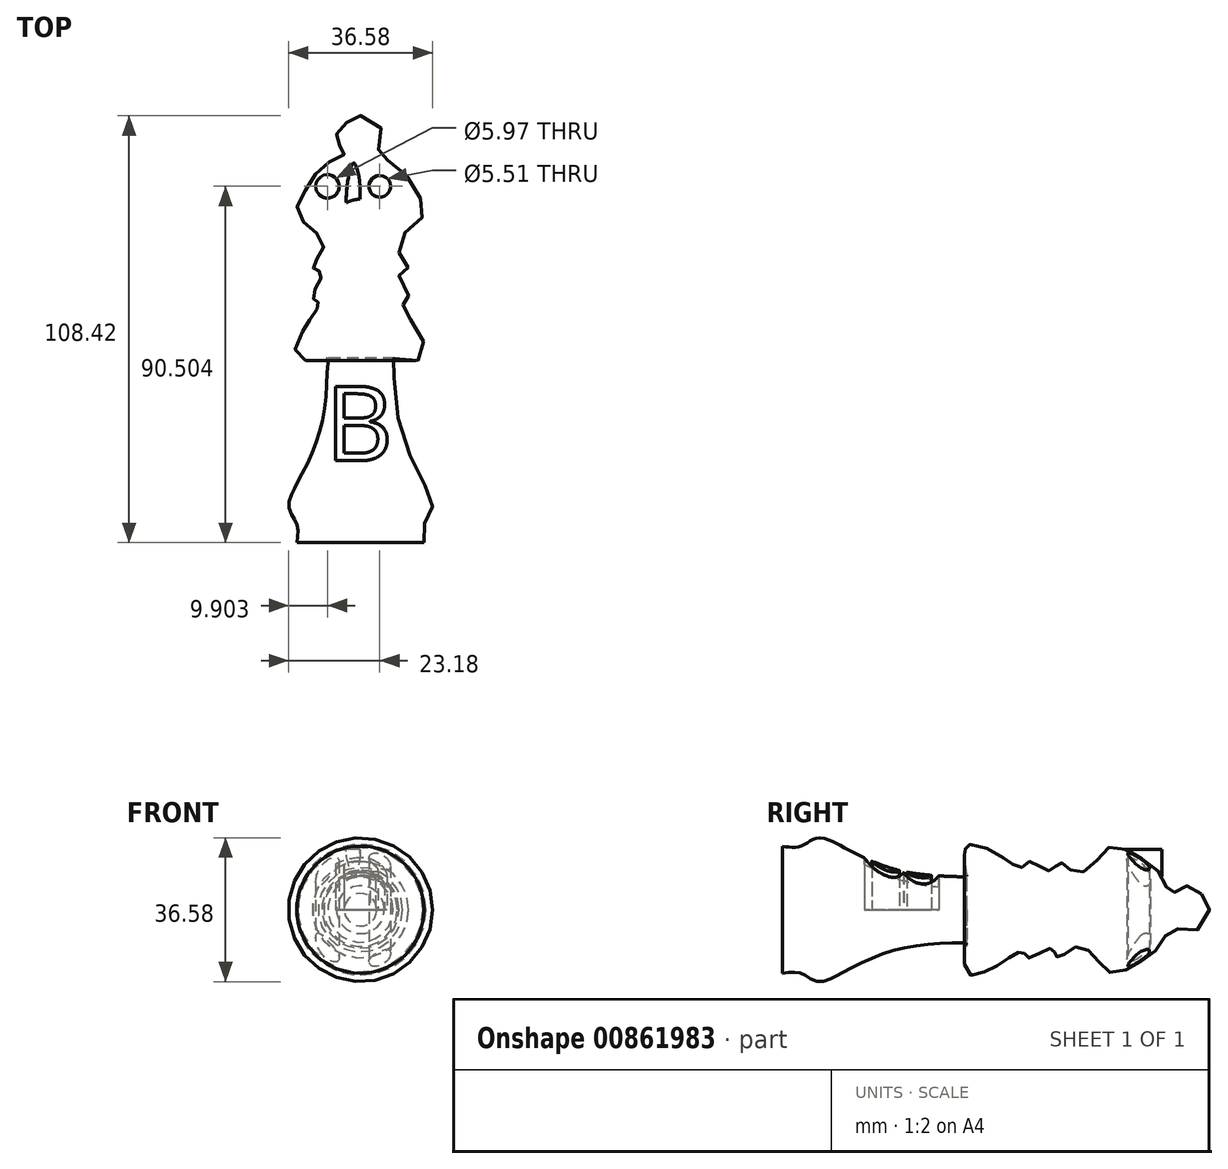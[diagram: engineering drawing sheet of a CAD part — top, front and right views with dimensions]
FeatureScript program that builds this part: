
annotation { "Feature Type Name" : "Feature", "Feature Type Description" : "" }
export const myFeature = defineFeature(function(context is Context, id is Id, definition is map)
    precondition{}
    {
        {
            var Q0;
            Q0=qCreatedBy(makeId("Top.planeOp"),FACE);
            var sketch = newSketch(context, id + "F0", { "sketchPlane" : qUnion([Q0])});
            skLineSegment(sketch, "E0", {"start": v(-40.03, 64.77) * mm, "end": v(-40.03, -59.56) * mm});
            skLineSegment(sketch, "E1", {"start": v(-40.03, -49.87) * mm, "end": v(-23.88, -49.87) * mm});
            skFitSpline(sketch, "E2", {"points": [v(-23.88, -49.87) * mm, v(-23.88, -45.26) * mm, v(-21.8, -41.1) * mm, v(-23.88, -34.88) * mm, v(-30.34, -18.96) * mm, v(-31.72, -3.74) * mm, v(-31.5, -3.05) * mm, v(-23.88, -3.05) * mm, v(-26.19, 5.26) * mm, v(-28.26, 8.26) * mm, v(-29.19, 11.26) * mm, v(-27.8, 12.4) * mm, v(-30.1, 17.71) * mm, v(-29.65, 19.1) * mm, v(-27.8, 20.25) * mm, v(-30.57, 24.63) * mm, v(-27.57, 29.94) * mm, v(-23.88, 33.86) * mm, v(-26.42, 40.32) * mm, v(-31.96, 46.78) * mm, v(-35.88, 48.85) * mm, v(-34.03, 54.16) * mm, v(-40.03, 58.54) * mm, v(-40.03, 58.31) * mm], "startDerivative": vector(-18.45, 115.41) * mm, "endDerivative": vector(14.43, -32.83) * mm});
            skSolve(sketch);
        }
        {
            var Q0;
            {var subQ4=sQuery(id+"F0.wireOp",EDGE,"E1");Q0=makeQuery(id+"F0.imprint","IMPRINT",FACE,{"disambiguationData":[TD([[makeQuery(id+"F0.imprint","IMPRINT",EDGE,{"derivedFrom":subQ4}),1.0]])]});}
            var Q1;
            Q1=sQuery(id+"F0.wireOp",EDGE,"E0");
            revolve(context, id + "F1", {"entities" : qUnion([Q0]), "axis" : qUnion([Q1]), "revolveType" : RevolveType.FULL});
        }
        {
            var Q0;
            Q0=qCreatedBy(makeId("Top.planeOp"),FACE);
            var sketch = newSketch(context, id + "F2", { "sketchPlane" : qUnion([Q0])});
            skCircle(sketch, "E3", {"center": v(-35.14, 40.63) * mm, "radius": 2.76 * mm});
            skCircle(sketch, "E4", {"center": v(-48.42, 40.63) * mm, "radius": 2.98 * mm});
            skFitSpline(sketch, "E5", {"points": [v(-42.24, 44.98) * mm, v(-42.7, 40.86) * mm, v(-42.7, 36.74) * mm, v(-39.72, 36.97) * mm], "startDerivative": vector(-0.93, -10.8) * mm, "endDerivative": vector(12.36, 3.86) * mm});
            skFitSpline(sketch, "E6", {"points": [v(-39.72, 36.97) * mm, v(-42.35, 43.72) * mm], "startDerivative": vector(-2.63, 6.75) * mm, "endDerivative": vector(-2.63, 6.75) * mm});
            skSolve(sketch);
        }
        {
            var Q0;
            Q0 = qSketchRegion(id + "F2", true);
            extrude(context, id + "F3", {"entities" : qUnion([Q0]), "operationType" : NewBodyOperationType.REMOVE, "depth" : 36.8 * mm, "offsetDistance" : 25 * mm, "hasSecondDirection" : true, "secondDirectionOppositeDirection" : true, "secondDirectionDepth" : 44.2 * mm});
        }
        {
            var Q0;
            Q0=qCreatedBy(makeId("Top.planeOp"),FACE);
            var sketch = newSketch(context, id + "F4", { "sketchPlane" : qUnion([Q0])});
            skText(sketch, "E7", { "text": "B", "fontName": "OpenSans-Regular.ttf"});
            const initialGuessF4  = {"E7": [-0.04896, -0.02906, 1, 0, 0.01905]};
            skSetInitialGuess(sketch, initialGuessF4);
            skSolve(sketch);
        }
        {
            var Q0;
            Q0 = qSketchRegion(id + "F4", true);
            extrude(context, id + "F5", {"entities" : qUnion([Q0]), "operationType" : NewBodyOperationType.REMOVE, "depth" : 64.5 * mm, "offsetDistance" : 25 * mm});
        }
        {
            var Q0;
            Q0=qCreatedBy(makeId("Top.planeOp"),FACE);
            var sketch = newSketch(context, id + "F6", { "sketchPlane" : qUnion([Q0])});
            skFitSpline(sketch, "E8", {"points": [v(-41.64, 46.54) * mm, v(-43.64, 38.2) * mm, v(-42.73, 34.93) * mm, v(-40.55, 35.84) * mm, v(-41.64, 46.54) * mm]});
            skSolve(sketch);
        }
        {
            var Q0;
            Q0 = qSketchRegion(id + "F6", true);
            extrude(context, id + "F7", {"entities" : qUnion([Q0]), "operationType" : NewBodyOperationType.ADD, "depth" : 15.3 * mm, "offsetDistance" : 25 * mm});
        }
    });
